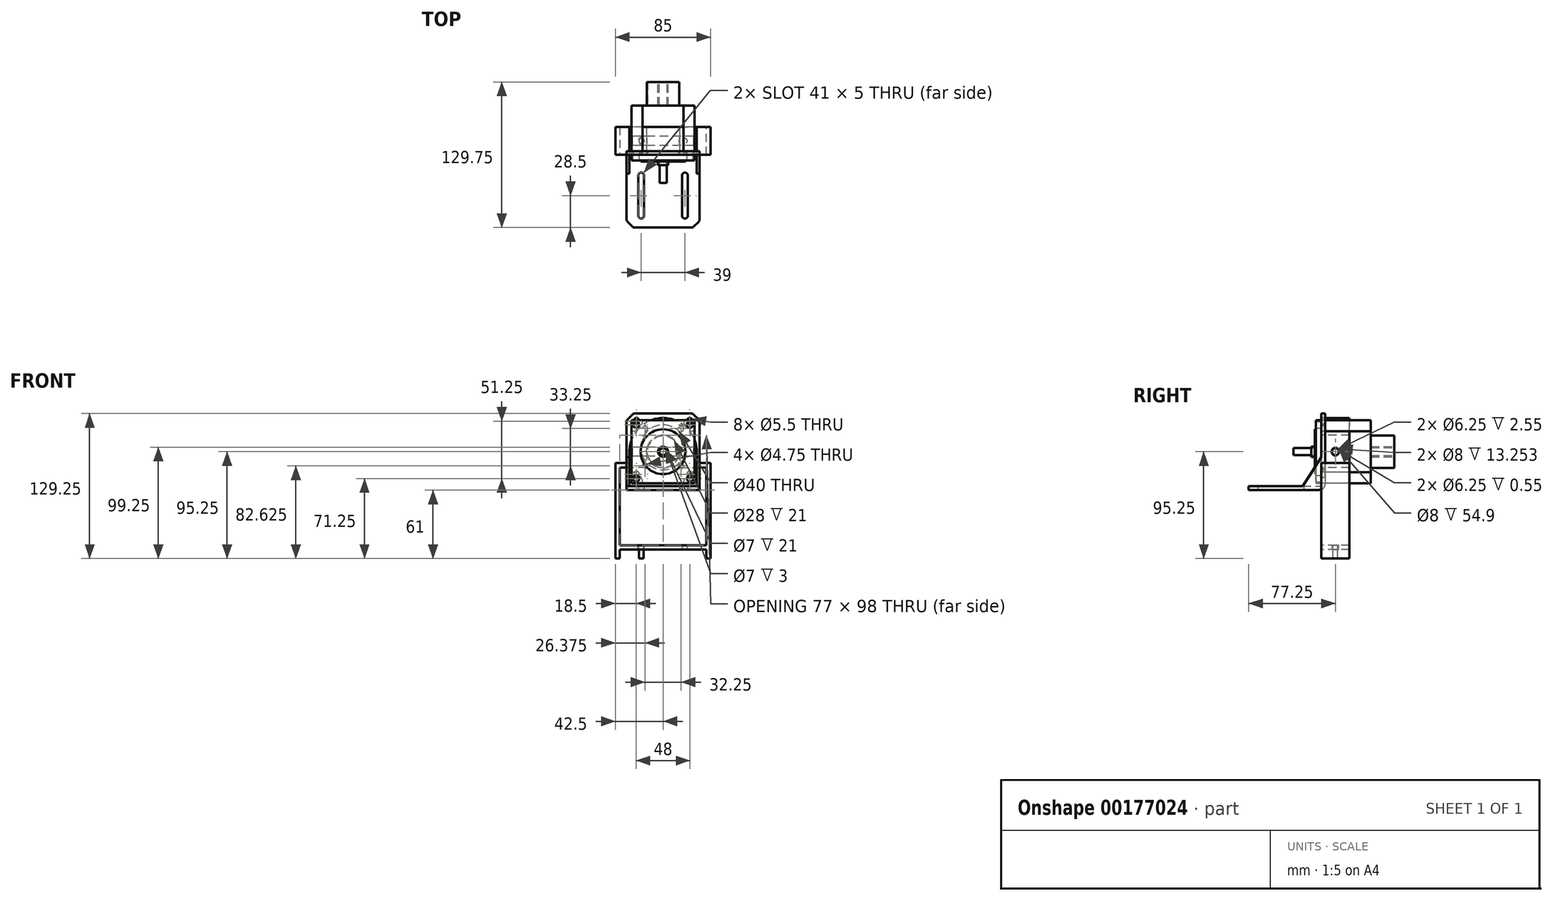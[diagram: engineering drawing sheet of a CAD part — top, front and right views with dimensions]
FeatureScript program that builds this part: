
annotation { "Feature Type Name" : "Feature", "Feature Type Description" : "" }
export const myFeature = defineFeature(function(context is Context, id is Id, definition is map)
    precondition{}
    {
        {
            var Q0;
            Q0=qCreatedBy(makeId("Front.planeOp"),FACE);
            var sketch = newSketch(context, id + "F0", { "sketchPlane" : qUnion([Q0])});
            skCircle(sketch, "E0", {"center": v(0, 0) * mm, "radius": 14 * mm});
            skCircle(sketch, "E1", {"center": v(0, 0) * mm, "radius": 14.5 * mm});
            skCircle(sketch, "E2", {"center": v(0, 0) * mm, "radius": 4.5 * mm});
            skCircle(sketch, "E3", {"center": v(0, 0) * mm, "radius": 3.5 * mm});
            skCircle(sketch, "E4", {"center": v(0, 0) * mm, "radius": 33 * mm});
            skCircle(sketch, "E5", {"center": v(0, 0) * mm, "radius": 35.5 * mm});
            skSolve(sketch);
        }
        {
            var Q0;
            Q0=makeQuery(id+"F0.imprint","IMPRINT",FACE,{"disambiguationData":[TD([[makeQuery(id+"F0.imprint","IMPRINT",EDGE,{"derivedFrom":sQuery(id+"F0.wireOp",EDGE,"E2")}),1.0]])]});
            extrude(context, id + "F1", {"entities" : qUnion([Q0]), "depth" : 9 * mm, "hasSecondDirection" : true, "secondDirectionOppositeDirection" : true, "secondDirectionDepth" : 65 * mm});
        }
        {
            var Q0;
            Q0=makeQuery(id+"F0.imprint","IMPRINT",FACE,{"disambiguationData":[TD([[makeQuery(id+"F0.imprint","IMPRINT",EDGE,{"derivedFrom":sQuery(id+"F0.wireOp",EDGE,"E0")}),-1.0]])]});
            extrude(context, id + "F2", {"entities" : qUnion([Q0]), "oppositeDirection" : true, "depth" : 65 * mm});
        }
        {
            var Q0;
            Q0=qCreatedBy(makeId("Front.planeOp"),FACE);
            var sketch = newSketch(context, id + "F3", { "sketchPlane" : qUnion([Q0])});
            skLineSegment(sketch, "E6.bottom", {"start": v(-28, 28) * mm, "end": v(28, 28) * mm});
            skLineSegment(sketch, "E6.top", {"start": v(-28, -28) * mm, "end": v(28, -28) * mm});
            skLineSegment(sketch, "E6.left", {"start": v(-28, 28) * mm, "end": v(-28, -28) * mm});
            skLineSegment(sketch, "E6.right", {"start": v(28, 28) * mm, "end": v(28, -28) * mm});
            skCircle(sketch, "E7", {"center": v(0, 0) * mm, "radius": 2.5 * mm});
            skCircle(sketch, "E8", {"center": v(0, 0) * mm, "radius": 20 * mm});
            skCircle(sketch, "E9", {"center": v(24, 24) * mm, "radius": 2.75 * mm});
            skCircle(sketch, "E10", {"center": v(-24, 24) * mm, "radius": 2.75 * mm});
            skCircle(sketch, "E11", {"center": v(-24, -24) * mm, "radius": 2.75 * mm});
            skCircle(sketch, "E12", {"center": v(24, -24) * mm, "radius": 2.75 * mm});
            skArc(sketch, "E13", {"start": v(18.19, 28) * mm, "mid": v(21.06, 21.06) * mm, "end": v(28, 18.19) * mm});
            skArc(sketch, "E14.1.0", {"start": v(28, -18.19) * mm, "mid": v(21.06, -21.06) * mm, "end": v(18.19, -28) * mm});
            skArc(sketch, "E14.2.0", {"start": v(-18.19, -28) * mm, "mid": v(-21.06, -21.06) * mm, "end": v(-28, -18.19) * mm});
            skArc(sketch, "E14.3.0", {"start": v(-28, 18.19) * mm, "mid": v(-21.06, 21.06) * mm, "end": v(-18.19, 28) * mm});
            skLineSegment(sketch, "E14.anchor1", {"start": v(0, 0) * mm, "end": v(28, 18.19) * mm, "construction": true});
            skLineSegment(sketch, "E14.anchor2", {"start": v(0, 0) * mm, "end": v(-18.19, 28) * mm, "construction": true});
            skSolve(sketch);
        }
        {
            var Q0;
            Q0=makeQuery(id+"F3.imprint","IMPRINT",FACE,{"disambiguationData":[TD([[makeQuery(id+"F3.imprint","IMPRINT",EDGE,{"derivedFrom":sQuery(id+"F3.wireOp",EDGE,"E8")}),-1.0]])]});
            var Q1;
            Q1=makeQuery(id+"F3.imprint","IMPRINT",FACE,{"disambiguationData":[TD([[makeQuery(id+"F3.imprint","IMPRINT",EDGE,{"derivedFrom":sQuery(id+"F3.wireOp",EDGE,"E7")}),1.0]])]});
            var Q2;
            Q2=makeQuery(id+"F3.imprint","IMPRINT",FACE,{"disambiguationData":[TD([[makeQuery(id+"F3.imprint","IMPRINT",EDGE,{"derivedFrom":sQuery(id+"F3.wireOp",EDGE,"E7")}),-1.0]])]});
            extrude(context, id + "F4", {"entities" : qUnion([Q0, Q1, Q2]), "oppositeDirection" : true, "depth" : 44 * mm});
        }
        {
            var Q0;
            Q0 = qSketchRegion(id + "F3", true);
            var Q1;
            Q1=makeQuery(id+"F4.opExtrude","CAP_FACE",FACE,{"disambiguationData":[OSD([sQuery(id+"F3.wireOp",EDGE,"E6.bottom"),sQuery(id+"F3.wireOp",EDGE,"E6.top"),sQuery(id+"F3.wireOp",EDGE,"E6.left"),sQuery(id+"F3.wireOp",EDGE,"E6.right"),sQuery(id+"F3.wireOp",EDGE,"E13"),sQuery(id+"F3.wireOp",EDGE,"E14.1.0"),sQuery(id+"F3.wireOp",EDGE,"E14.2.0"),sQuery(id+"F3.wireOp",EDGE,"E14.3.0")])],"isStart":true});
            extrude(context, id + "F5", {"entities" : qUnion([Q0, Q1]), "operationType" : NewBodyOperationType.ADD, "depth" : 5 * mm});
        }
        {
            var Q0;
            {var subQ0=sQuery(id+"F3.wireOp",EDGE,"E6.right");var subQ1=sQuery(id+"F3.wireOp",EDGE,"E6.left");var subQ2=sQuery(id+"F3.wireOp",EDGE,"E6.top");var subQ3=sQuery(id+"F3.wireOp",EDGE,"E6.bottom");Q0=makeQuery(id+"F5.boolean.opBoolean","MERGE",FACE,{"derivedFrom":[makeQuery(id+"F5.opExtrude","CAP_FACE",FACE,{"disambiguationData":[OSD([subQ3,subQ2,subQ1,subQ0,sQuery(id+"F3.wireOp",EDGE,"E8"),sQuery(id+"F3.wireOp",EDGE,"E9"),sQuery(id+"F3.wireOp",EDGE,"E10"),sQuery(id+"F3.wireOp",EDGE,"E11"),sQuery(id+"F3.wireOp",EDGE,"E12")])],"isStart":false}),makeQuery(id+"F5.opExtrude","CAP_FACE",FACE,{"disambiguationData":[OSD([subQ3,subQ2,subQ1,subQ0,sQuery(id+"F3.wireOp",EDGE,"E13"),sQuery(id+"F3.wireOp",EDGE,"E14.1.0"),sQuery(id+"F3.wireOp",EDGE,"E14.2.0"),sQuery(id+"F3.wireOp",EDGE,"E14.3.0")])],"isStart":false})]});}
            var sketch = newSketch(context, id + "F6", { "sketchPlane" : qUnion([Q0])});
            skCircle(sketch, "E15", {"center": v(0, 0) * mm, "radius": 20 * mm});
            skSolve(sketch);
        }
        {
            var Q0;
            Q0 = qSketchRegion(id + "F6", true);
            extrude(context, id + "F7", {"entities" : qUnion([Q0]), "operationType" : NewBodyOperationType.ADD, "depth" : 1 * mm});
        }
        {
            var Q0;
            Q0=makeQuery(id+"F7.opExtrude","CAP_FACE",FACE,{"disambiguationData":[OSD([sQuery(id+"F6.wireOp",EDGE,"E15")])],"isStart":false});
            var sketch = newSketch(context, id + "F8", { "sketchPlane" : qUnion([Q0])});
            skCircle(sketch, "E16", {"center": v(0, 0) * mm, "radius": 3.17 * mm});
            skSolve(sketch);
        }
        {
            var Q0;
            Q0 = qSketchRegion(id + "F8", true);
            extrude(context, id + "F9", {"entities" : qUnion([Q0]), "operationType" : NewBodyOperationType.ADD, "depth" : 19 * mm});
        }
        {
            var Q0;
            Q0=qCreatedBy(makeId("Front.planeOp"),FACE);
            var sketch = newSketch(context, id + "F10", { "sketchPlane" : qUnion([Q0])});
            skLineSegment(sketch, "E17", {"start": v(-32.5, 28) * mm, "end": v(-26.5, 34) * mm});
            skLineSegment(sketch, "E18", {"start": v(26.5, 34) * mm, "end": v(32.5, 28) * mm});
            skPoint(sketch, "E19.orphan", {"position": v(-32.5, 34) * mm});
            skPoint(sketch, "E20.orphan", {"position": v(32.5, 34) * mm});
            skLineSegment(sketch, "E21.bottom", {"start": v(-26.5, 34) * mm, "end": v(26.5, 34) * mm});
            skLineSegment(sketch, "E21.top", {"start": v(-32.5, -34) * mm, "end": v(32.5, -34) * mm});
            skLineSegment(sketch, "E21.left", {"start": v(-32.5, 28) * mm, "end": v(-32.5, -34) * mm});
            skLineSegment(sketch, "E21.right", {"start": v(32.5, 28) * mm, "end": v(32.5, -34) * mm});
            skCircle(sketch, "E22", {"center": v(0, 4) * mm, "radius": 20 * mm});
            skCircle(sketch, "E23", {"center": v(23.75, 27.25) * mm, "radius": 2.75 * mm});
            skCircle(sketch, "E24", {"center": v(23.75, -20.25) * mm, "radius": 2.75 * mm});
            skCircle(sketch, "E25", {"center": v(-23.75, 27.25) * mm, "radius": 2.75 * mm});
            skCircle(sketch, "E26", {"center": v(-23.75, -20.25) * mm, "radius": 2.75 * mm});
            skCircle(sketch, "E27", {"center": v(16.12, 20.63) * mm, "radius": 2.37 * mm});
            skCircle(sketch, "E28", {"center": v(-16.12, -12.62) * mm, "radius": 2.37 * mm});
            skCircle(sketch, "E29", {"center": v(-16.12, 20.62) * mm, "radius": 2.37 * mm});
            skCircle(sketch, "E30", {"center": v(16.12, -12.62) * mm, "radius": 2.37 * mm});
            skSolve(sketch);
        }
        {
            var Q0;
            Q0 = qSketchRegion(id + "F10", true);
            extrude(context, id + "F11", {"entities" : qUnion([Q0]), "oppositeDirection" : true, "depth" : 3.25 * mm});
        }
        {
            var Q0;
            Q0=makeQuery(id+"F11.opExtrude","SWEPT_FACE",FACE,{"disambiguationData":[OSD([sQuery(id+"F10.wireOp",EDGE,"E21.top")])]});
            var sketch = newSketch(context, id + "F12", { "sketchPlane" : qUnion([Q0])});
            skLineSegment(sketch, "E31.bottom", {"start": v(-26.5, 64.75) * mm, "end": v(26.5, 64.75) * mm});
            skLineSegment(sketch, "E31.top", {"start": v(-32.5, 0) * mm, "end": v(32.5, 0) * mm});
            skLineSegment(sketch, "E31.left", {"start": v(-32.5, 58.75) * mm, "end": v(-32.5, 0) * mm});
            skLineSegment(sketch, "E31.right", {"start": v(32.5, 58.75) * mm, "end": v(32.5, 0) * mm});
            skLineSegment(sketch, "E32", {"start": v(-32.5, 58.75) * mm, "end": v(-26.5, 64.75) * mm});
            skLineSegment(sketch, "E33", {"start": v(26.5, 64.75) * mm, "end": v(32.5, 58.75) * mm});
            skLineSegment(sketch, "E34.left", {"start": v(-22, 54.25) * mm, "end": v(-22, 18.25) * mm});
            skLineSegment(sketch, "E34.right", {"start": v(-17, 54.25) * mm, "end": v(-17, 18.25) * mm});
            skArc(sketch, "E35", {"start": v(-17, 54.25) * mm, "mid": v(-19.5, 56.75) * mm, "end": v(-22, 54.25) * mm});
            skArc(sketch, "E36.MirrorCS", {"start": v(-17, 18.25) * mm, "mid": v(-19.5, 15.75) * mm, "end": v(-22, 18.25) * mm});
            skArc(sketch, "E37.MirrorCS", {"start": v(17, 54.25) * mm, "mid": v(19.5, 56.75) * mm, "end": v(22, 54.25) * mm});
            skLineSegment(sketch, "E38.MirrorCS", {"start": v(22, 54.25) * mm, "end": v(22, 18.25) * mm});
            skLineSegment(sketch, "E39.MirrorCS", {"start": v(17, 54.25) * mm, "end": v(17, 18.25) * mm});
            skArc(sketch, "E40.MirrorCS", {"start": v(17, 18.25) * mm, "mid": v(19.5, 15.75) * mm, "end": v(22, 18.25) * mm});
            skSolve(sketch);
        }
        {
            var Q0;
            Q0 = qSketchRegion(id + "F12", true);
            extrude(context, id + "F13", {"entities" : qUnion([Q0]), "operationType" : NewBodyOperationType.ADD, "oppositeDirection" : true, "depth" : 3.5 * mm});
        }
        {
            var Q0;
            Q0=makeQuery(id+"F13.boolean.opBoolean","MERGE",FACE,{"derivedFrom":[makeQuery(id+"F11.opExtrude","SWEPT_FACE",FACE,{"disambiguationData":[OSD([sQuery(id+"F10.wireOp",EDGE,"E21.right")])]}),makeQuery(id+"F13.opExtrude","SWEPT_FACE",FACE,{"disambiguationData":[OSD([sQuery(id+"F12.wireOp",EDGE,"E31.right")])]})]});
            var sketch = newSketch(context, id + "F14", { "sketchPlane" : qUnion([Q0])});
            skLineSegment(sketch, "E41", {"start": v(0, -5) * mm, "end": v(-16.75, -30.5) * mm});
            skLineSegment(sketch, "E42", {"start": v(-16.75, -30.5) * mm, "end": v(0, -30.5) * mm});
            skLineSegment(sketch, "E43", {"start": v(0, -30.5) * mm, "end": v(0, -5) * mm});
            skSolve(sketch);
        }
        {
            var Q0;
            Q0 = qSketchRegion(id + "F14", true);
            extrude(context, id + "F15", {"entities" : qUnion([Q0]), "operationType" : NewBodyOperationType.ADD, "oppositeDirection" : true, "depth" : 2.5 * mm});
        }
        {
            var Q0;
            Q0=makeQuery(id+"F13.boolean.opBoolean","MERGE",FACE,{"derivedFrom":[makeQuery(id+"F11.opExtrude","SWEPT_FACE",FACE,{"disambiguationData":[OSD([sQuery(id+"F10.wireOp",EDGE,"E21.left")])]}),makeQuery(id+"F13.opExtrude","SWEPT_FACE",FACE,{"disambiguationData":[OSD([sQuery(id+"F12.wireOp",EDGE,"E31.left")])]})]});
            var sketch = newSketch(context, id + "F16", { "sketchPlane" : qUnion([Q0])});
            skLineSegment(sketch, "E44", {"start": v(0, -5) * mm, "end": v(16.75, -30.5) * mm});
            skLineSegment(sketch, "E45", {"start": v(16.75, -30.5) * mm, "end": v(0, -30.5) * mm});
            skLineSegment(sketch, "E46", {"start": v(0, -30.5) * mm, "end": v(0, -5) * mm});
            skSolve(sketch);
        }
        {
            var Q0;
            Q0 = qSketchRegion(id + "F16", true);
            extrude(context, id + "F17", {"entities" : qUnion([Q0]), "operationType" : NewBodyOperationType.ADD, "oppositeDirection" : true, "depth" : 2.5 * mm});
        }
        {
            var Q0;
            Q0=makeQuery(id+"F11.opExtrude","SWEPT_EDGE",EDGE,{"disambiguationData":[OSD([sQuery(id+"F10.wireOp",EDGE,"E17"),sQuery(id+"F10.wireOp",EDGE,"E21.bottom")])]});
            var Q1;
            Q1=makeQuery(id+"F11.opExtrude","SWEPT_EDGE",EDGE,{"disambiguationData":[OSD([sQuery(id+"F10.wireOp",EDGE,"E17"),sQuery(id+"F10.wireOp",EDGE,"E21.left")])]});
            var Q2;
            Q2=makeQuery(id+"F11.opExtrude","SWEPT_EDGE",EDGE,{"disambiguationData":[OSD([sQuery(id+"F10.wireOp",EDGE,"E18"),sQuery(id+"F10.wireOp",EDGE,"E21.bottom")])]});
            var Q3;
            Q3=makeQuery(id+"F11.opExtrude","SWEPT_EDGE",EDGE,{"disambiguationData":[OSD([sQuery(id+"F10.wireOp",EDGE,"E18"),sQuery(id+"F10.wireOp",EDGE,"E21.right")])]});
            var Q4;
            Q4=makeQuery(id+"F13.opExtrude","SWEPT_EDGE",EDGE,{"disambiguationData":[OSD([sQuery(id+"F12.wireOp",EDGE,"E31.left"),sQuery(id+"F12.wireOp",EDGE,"E32")])]});
            var Q5;
            Q5=makeQuery(id+"F13.opExtrude","SWEPT_EDGE",EDGE,{"disambiguationData":[OSD([sQuery(id+"F12.wireOp",EDGE,"E31.bottom"),sQuery(id+"F12.wireOp",EDGE,"E32")])]});
            var Q6;
            Q6=makeQuery(id+"F13.opExtrude","SWEPT_EDGE",EDGE,{"disambiguationData":[OSD([sQuery(id+"F12.wireOp",EDGE,"E31.bottom"),sQuery(id+"F12.wireOp",EDGE,"E33")])]});
            var Q7;
            Q7=makeQuery(id+"F13.opExtrude","SWEPT_EDGE",EDGE,{"disambiguationData":[OSD([sQuery(id+"F12.wireOp",EDGE,"E31.right"),sQuery(id+"F12.wireOp",EDGE,"E33")])]});
            fillet(context, id + "F18", {"entities" : qUnion([Q0, Q1, Q2, Q3, Q4, Q5, Q6, Q7]), "radius" : 2.5 * mm, "tangentPropagation" : true, "allowEdgeOverflow" : false});
        }
        {
            var Q0;
            Q0=makeQuery(id+"F11.opExtrude","CAP_EDGE",EDGE,{"disambiguationData":[OSD([sQuery(id+"F10.wireOp",EDGE,"E21.top")])],"isStart":false});
            fillet(context, id + "F19", {"entities" : qUnion([Q0]), "radius" : 5 * mm, "tangentPropagation" : true, "allowEdgeOverflow" : false});
        }
        {
            var Q0;
            Q0=qCreatedBy(makeId("Front.planeOp"),FACE);
            var sketch = newSketch(context, id + "F20", { "sketchPlane" : qUnion([Q0])});
            skArc(sketch, "E47", {"start": v(30, 0) * mm, "mid": v(0, 30) * mm, "end": v(-30, 0) * mm});
            skArc(sketch, "E48", {"start": v(14.75, 0) * mm, "mid": v(0, 14.75) * mm, "end": v(-14.75, 0) * mm});
            skLineSegment(sketch, "E49", {"start": v(-30, 0) * mm, "end": v(-30, -10) * mm});
            skLineSegment(sketch, "E50", {"start": v(-30, -10) * mm, "end": v(-42.5, -10) * mm});
            skLineSegment(sketch, "E51", {"start": v(-14.75, 0) * mm, "end": v(-14.75, -14) * mm});
            skLineSegment(sketch, "E52", {"start": v(-14.75, -14) * mm, "end": v(-38.5, -14) * mm});
            skLineSegment(sketch, "E53", {"start": v(-42.5, -10) * mm, "end": v(-42.5, -95.25) * mm});
            skLineSegment(sketch, "E54", {"start": v(-38.5, -14) * mm, "end": v(-38.5, -83.25) * mm});
            skPoint(sketch, "E55.endSnap0", {"position": v(0, 14.75) * mm});
            skLineSegment(sketch, "E56.MirrorCS", {"start": v(14.75, -14) * mm, "end": v(38.5, -14) * mm});
            skLineSegment(sketch, "E57.MirrorCS", {"start": v(30, -10) * mm, "end": v(42.5, -10) * mm});
            skLineSegment(sketch, "E58.MirrorCS", {"start": v(42.5, -10) * mm, "end": v(42.5, -95.25) * mm});
            skLineSegment(sketch, "E59.MirrorCS", {"start": v(14.75, 0) * mm, "end": v(14.75, -14) * mm});
            skLineSegment(sketch, "E60.MirrorCS", {"start": v(30, 0) * mm, "end": v(30, -10) * mm});
            skLineSegment(sketch, "E61.MirrorCS", {"start": v(38.5, -14) * mm, "end": v(38.5, -83.25) * mm});
            skLineSegment(sketch, "E62", {"start": v(-38.5, -83.25) * mm, "end": v(38.5, -83.25) * mm});
            skLineSegment(sketch, "E63", {"start": v(-42.5, -95.25) * mm, "end": v(42.5, -95.25) * mm});
            skSolve(sketch);
        }
        {
            var Q0;
            Q0 = qSketchRegion(id + "F20", true);
            extrude(context, id + "F21", {"entities" : qUnion([Q0]), "oppositeDirection" : true, "depth" : 25 * mm});
        }
        {
            var Q0;
            Q0=makeQuery(id+"F21.opExtrude","SWEPT_FACE",FACE,{"disambiguationData":[OSD([sQuery(id+"F20.wireOp",EDGE,"E60.MirrorCS")])]});
            var sketch = newSketch(context, id + "F22", { "sketchPlane" : qUnion([Q0])});
            skPoint(sketch, "E64.centerSnap0", {"position": v(12.5, -10) * mm});
            skCircle(sketch, "E65", {"center": v(12.5, 0) * mm, "radius": 3.12 * mm});
            skSolve(sketch);
        }
        {
            var Q0;
            {var subQ0=sQuery(id+"F22.wireOp",EDGE,"E65");var subQ1=makeQuery(id+"F21.opExtrude","SWEPT_EDGE",EDGE,{"disambiguationData":[OSD([sQuery(id+"F20.wireOp",EDGE,"E47"),sQuery(id+"F20.wireOp",EDGE,"E60.MirrorCS")])]});var subQ2=makeQuery(id+"F22.imprint","INTERSECT",VERTEX,{"disambiguationData":[OD(0.0)],"derivedFrom":[subQ1,subQ0]});Q0=makeQuery(id+"F22.imprint","IMPRINT",FACE,{"disambiguationData":[TD([[makeQuery(id+"F22.imprint","IMPRINT",EDGE,{"disambiguationData":[TD([[subQ2,-1.0]])],"derivedFrom":subQ0}),1.0]])]});}
            var Q1;
            {var subQ0=sQuery(id+"F22.wireOp",EDGE,"E65");var subQ1=makeQuery(id+"F21.opExtrude","SWEPT_EDGE",EDGE,{"disambiguationData":[OSD([sQuery(id+"F20.wireOp",EDGE,"E47"),sQuery(id+"F20.wireOp",EDGE,"E60.MirrorCS")])]});var subQ2=makeQuery(id+"F22.imprint","INTERSECT",VERTEX,{"disambiguationData":[OD(0.0)],"derivedFrom":[subQ1,subQ0]});Q1=makeQuery(id+"F22.imprint","IMPRINT",FACE,{"disambiguationData":[TD([[makeQuery(id+"F22.imprint","IMPRINT",EDGE,{"disambiguationData":[TD([[subQ2,1.0]])],"derivedFrom":subQ0}),1.0]])]});}
            extrude(context, id + "F23", {"entities" : qUnion([Q0, Q1]), "operationType" : NewBodyOperationType.REMOVE, "endBound" : BoundingType.THROUGH_ALL, "oppositeDirection" : true, "depth" : 100 * mm});
        }
        {
            var Q0;
            Q0=makeQuery(id+"F21.opExtrude","SWEPT_FACE",FACE,{"disambiguationData":[OSD([sQuery(id+"F20.wireOp",EDGE,"E59.MirrorCS")])]});
            var sketch = newSketch(context, id + "F24", { "sketchPlane" : qUnion([Q0])});
            skCircle(sketch, "E66", {"center": v(-12.5, 0) * mm, "radius": 4 * mm});
            skCircle(sketch, "E67", {"center": v(-12.5, 0) * mm, "radius": 1.03 * mm});
            skSolve(sketch);
        }
        {
            var Q0;
            Q0 = qSketchRegion(id + "F24", true);
            extrude(context, id + "F25", {"entities" : qUnion([Q0]), "operationType" : NewBodyOperationType.REMOVE, "oppositeDirection" : true, "depth" : 12.7 * mm, "hasSecondDirection" : true, "secondDirectionOppositeDirection" : false, "secondDirectionDepth" : 42.2 * mm});
        }
        {
            var Q0;
            Q0=makeQuery(id+"F21.opExtrude","SWEPT_FACE",FACE,{"disambiguationData":[OSD([sQuery(id+"F20.wireOp",EDGE,"E62")])]});
            var sketch = newSketch(context, id + "F26", { "sketchPlane" : qUnion([Q0])});
            skCircle(sketch, "E68", {"center": v(19.5, 12.5) * mm, "radius": 2.8 * mm});
            skCircle(sketch, "E69", {"center": v(19.5, 12.5) * mm, "radius": 2.12 * mm});
            skCircle(sketch, "E70.MirrorC", {"center": v(-19.5, 12.5) * mm, "radius": 2.8 * mm});
            skCircle(sketch, "E71.MirrorC", {"center": v(-19.5, 12.5) * mm, "radius": 2.12 * mm});
            skSolve(sketch);
        }
        {
            var Q0;
            Q0=makeQuery(id+"F26.imprint","IMPRINT",FACE,{"disambiguationData":[TD([[makeQuery(id+"F26.imprint","IMPRINT",EDGE,{"derivedFrom":sQuery(id+"F26.wireOp",EDGE,"E69")}),1.0]])]});
            var Q1;
            Q1=makeQuery(id+"F26.imprint","IMPRINT",FACE,{"disambiguationData":[TD([[makeQuery(id+"F26.imprint","IMPRINT",EDGE,{"derivedFrom":sQuery(id+"F26.wireOp",EDGE,"E71.MirrorC")}),-1.0]])]});
            var Q2;
            Q2=sQuery(id+"F26.wireOp",EDGE,"E69");
            var Q3;
            Q3=sQuery(id+"F26.wireOp",EDGE,"E71.MirrorC");
            extrude(context, id + "F27", {"entities" : qUnion([Q0, Q1]), "operationType" : NewBodyOperationType.REMOVE, "surfaceEntities" : qUnion([Q2, Q3]), "endBound" : BoundingType.THROUGH_ALL, "oppositeDirection" : true, "depth" : 25 * mm});
        }
        {
            var Q0;
            Q0=makeQuery(id+"F26.imprint","IMPRINT",FACE,{"disambiguationData":[TD([[makeQuery(id+"F26.imprint","IMPRINT",EDGE,{"derivedFrom":sQuery(id+"F26.wireOp",EDGE,"E68")}),1.0]])]});
            var Q1;
            Q1=makeQuery(id+"F26.imprint","IMPRINT",FACE,{"disambiguationData":[TD([[makeQuery(id+"F26.imprint","IMPRINT",EDGE,{"derivedFrom":sQuery(id+"F26.wireOp",EDGE,"E70.MirrorC")}),-1.0]])]});
            var Q2;
            Q2=sQuery(id+"F26.wireOp",EDGE,"E68");
            var Q3;
            Q3=sQuery(id+"F26.wireOp",EDGE,"E70.MirrorC");
            extrude(context, id + "F28", {"entities" : qUnion([Q0, Q1]), "operationType" : NewBodyOperationType.REMOVE, "surfaceEntities" : qUnion([Q2, Q3]), "endBound" : BoundingType.THROUGH_ALL, "oppositeDirection" : true, "depth" : 25 * mm, "hasSecondDirection" : true, "secondDirectionOppositeDirection" : true, "secondDirectionDepth" : 4 * mm});
        }
    });
